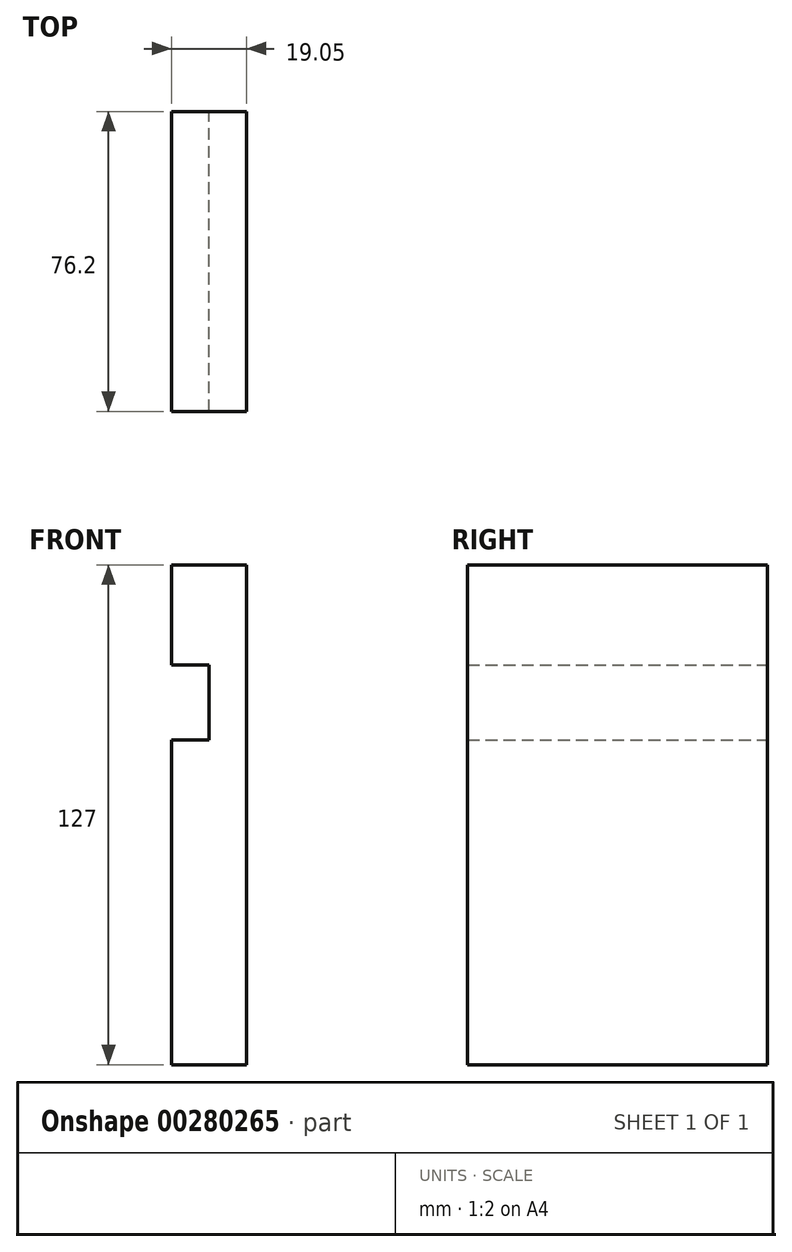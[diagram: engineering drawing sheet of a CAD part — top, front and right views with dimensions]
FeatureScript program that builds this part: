
annotation { "Feature Type Name" : "Feature", "Feature Type Description" : "" }
export const myFeature = defineFeature(function(context is Context, id is Id, definition is map)
    precondition{}
    {
        {
            var Q0;
            Q0=qCreatedBy(makeId("Front.planeOp"),FACE);
            var sketch = newSketch(context, id + "F0", { "sketchPlane" : qUnion([Q0])});
            skLineSegment(sketch, "E0", {"start": v(0, 0) * mm, "end": v(0, 127) * mm});
            skLineSegment(sketch, "E1", {"start": v(0, 127) * mm, "end": v(-19.05, 127) * mm});
            skLineSegment(sketch, "E2", {"start": v(-19.05, 127) * mm, "end": v(-19.05, 101.6) * mm});
            skLineSegment(sketch, "E3", {"start": v(-19.05, 101.6) * mm, "end": v(-9.52, 101.6) * mm});
            skLineSegment(sketch, "E4", {"start": v(-9.52, 101.6) * mm, "end": v(-9.52, 82.55) * mm});
            skLineSegment(sketch, "E5", {"start": v(-9.52, 82.55) * mm, "end": v(-19.05, 82.55) * mm});
            skLineSegment(sketch, "E6", {"start": v(-19.05, 82.55) * mm, "end": v(-19.05, 0) * mm});
            skLineSegment(sketch, "E7", {"start": v(-19.05, 0) * mm, "end": v(0, 0) * mm});
            skSolve(sketch);
        }
        {
            var Q0;
            Q0=makeQuery(id+"F0.imprint","IMPRINT",FACE,{"disambiguationData":[TD([[makeQuery(id+"F0.imprint","IMPRINT",EDGE,{"derivedFrom":sQuery(id+"F0.wireOp",EDGE,"E0")}),1.0]])]});
            extrude(context, id + "F1", {"entities" : qUnion([Q0]), "depth" : 76.2 * mm});
        }
    });
